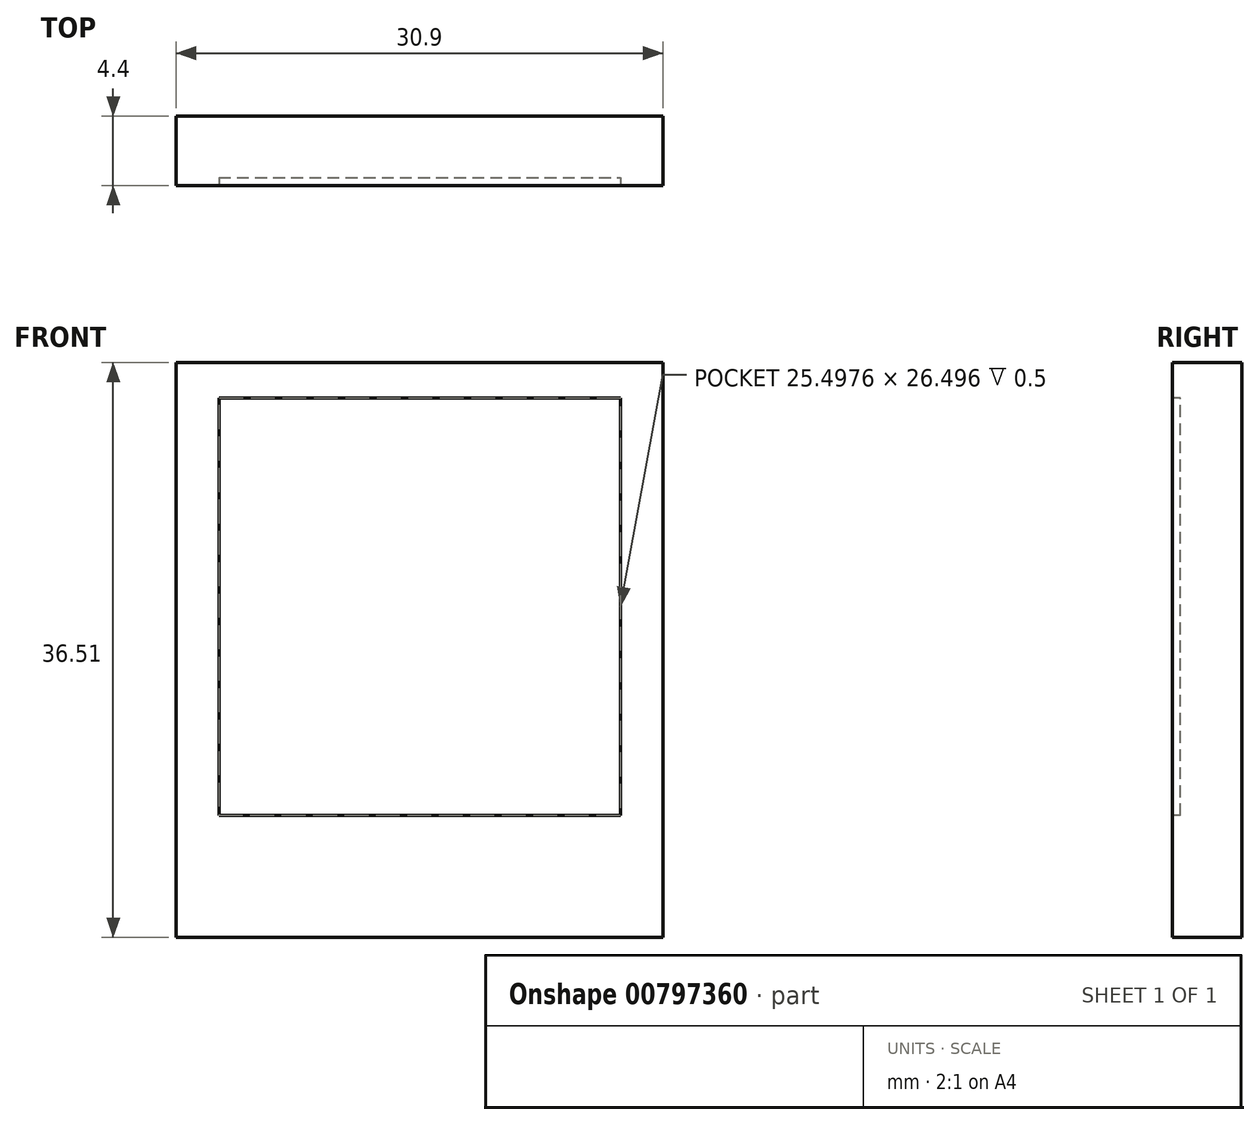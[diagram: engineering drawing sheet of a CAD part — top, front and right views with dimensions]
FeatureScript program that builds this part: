
annotation { "Feature Type Name" : "Feature", "Feature Type Description" : "" }
export const myFeature = defineFeature(function(context is Context, id is Id, definition is map)
    precondition{}
    {
        {
            var Q0;
            Q0=qCreatedBy(makeId("Front.planeOp"),FACE);
            var sketch = newSketch(context, id + "F0", { "sketchPlane" : qUnion([Q0])});
            skLineSegment(sketch, "E0.top", {"start": v(-15.45, 15.5) * mm, "end": v(15.45, 15.5) * mm});
            skLineSegment(sketch, "E0.left", {"start": v(-15.45, -21) * mm, "end": v(-15.45, 15.5) * mm});
            skLineSegment(sketch, "E0.right", {"start": v(15.45, -21) * mm, "end": v(15.45, 15.5) * mm});
            skLineSegment(sketch, "E1", {"start": v(-15.45, -21) * mm, "end": v(15.45, -21) * mm});
            skPoint(sketch, "E2", {"position": v(0, 0) * mm});
            skPoint(sketch, "E3", {"position": v(0, -21) * mm});
            skLineSegment(sketch, "E4", {"start": v(15.45, -21) * mm, "end": v(-15.45, 15.5) * mm, "construction": true});
            skPoint(sketch, "E5", {"position": v(0, -2.75) * mm});
            skSolve(sketch);
        }
        {
            var Q0;
            Q0=qSketchRegion(id+"F0",true);
            extrude(context, id + "F1", {"entities" : qUnion([Q0]), "depth" : 4.4 * mm, "offsetDistance" : 25 * mm});
        }
        {
            var Q0;
            Q0=makeQuery(id+"F1.opExtrude","CAP_FACE",FACE,{"disambiguationData":[OSD([sQuery(id+"F0.wireOp",EDGE,"E0.top"),sQuery(id+"F0.wireOp",EDGE,"E0.left"),sQuery(id+"F0.wireOp",EDGE,"E0.right"),sQuery(id+"F0.wireOp",EDGE,"E1")])],"isStart":false});
            var sketch = newSketch(context, id + "F2", { "sketchPlane" : qUnion([Q0])});
            skLineSegment(sketch, "E6.bottom", {"start": v(-12.75, -13.25) * mm, "end": v(12.75, -13.25) * mm});
            skLineSegment(sketch, "E6.top", {"start": v(-12.75, 13.25) * mm, "end": v(12.75, 13.25) * mm});
            skLineSegment(sketch, "E6.left", {"start": v(-12.75, -13.25) * mm, "end": v(-12.75, 13.25) * mm});
            skLineSegment(sketch, "E6.right", {"start": v(12.75, -13.25) * mm, "end": v(12.75, 13.25) * mm});
            skPoint(sketch, "E6.middle", {"position": v(0, 0) * mm});
            skSolve(sketch);
        }
        {
            var Q0;
            Q0 = qSketchRegion(id + "F2", true);
            extrude(context, id + "F3", {"entities" : qUnion([Q0]), "operationType" : NewBodyOperationType.REMOVE, "oppositeDirection" : true, "depth" : .5 * mm, "offsetDistance" : 25 * mm});
        }
    });
